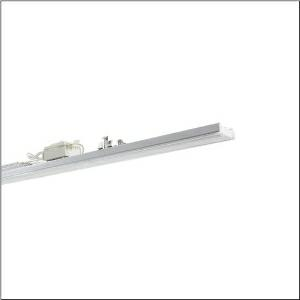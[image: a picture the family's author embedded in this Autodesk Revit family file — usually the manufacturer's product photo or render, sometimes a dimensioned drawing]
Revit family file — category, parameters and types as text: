
# Revit family: licross_11_recessed_ho_51tl1wmn4exm
name_source: partatom
category: Lighting Fixtures
units: mm (PartAtom-declared; Revit-internal decimal feet)

## family parameters
Cut with Voids When Loaded = No
Host = Face
Light Source = No
Part Type = Normal
Room Calculation Point = No
Round Connector Dimension = Use Diameter
Shared = No

## types (1)
- --- (1 x LED, 14240 lm, 74.5 W, 4000K)
    Apparent Load = 75 VA
    CIE Flux Codes = 73 94 99 100 100
    Color Rendering = 80
    Color Temperature = 4000K
    Default Elevation = 1800 mm
    Description = Licross 11 Recessed HO, luminaire insert, of sheet steel, coil coated, white, length: 1.500mm, width: 66mm, height: 67mm, LED rated luminous flux: 14.240lm, light colour: 840, SDCM (Standard Deviation of Colour Matching)MacAdam ≤ 2 SDCM (initial), control gear: ON/OFF Multilumen, with plug, 3-pole, with phase selection, mains connection: 220..240V, AC, 50/60Hz, rated input power: 75W, internal wiring halogen-free, primary optical cover: cover, of PMMA, light emission: direct distribution, primary light characteristic: symmetric, protection rating (complete): IP40, insulation class (complete): insulation class I (protective earthing), certification: CE, ENEC, VDE, UKCA, protection symbol: D if used in an environment without relevant dust loads with corresponding accessories, impact resistance: IK06, permissible ambient temperature for indoor applications: -35..+35°C, corresponds to IFS (International Featured Standards) requirements for safety and quality in the food industry, reducing of maximum allowable ambient temperature of 5°C with ceiling mounting, The light source and the operating device comply with the requirements of the Ecodesign Regulation (EU) 2019/2020 and are replaceable in accordance with this regulation, packaging unit: 1 piece
    Height = 58 mm
    Lamp = 1 x LED
    Lamp Light Flux = 14240 lm
    Lamp Power = 74.5 W
    Lamp count = 1
    Length = 1500 mm
    Luminous efficacy = 191 lm/W
    Manufacturer = Siteco
    ModVariant = No
    Model = 51TL1WMN4EXM
    Mounting Place = Ceiling
    Mounting Type = Pendant
    Number of Poles = 1
    OnlyDefault = Yes
    Power Factor = 1
    Product Name = Licross 11 Recessed HO
    Product group = luminaire insert | ceiling pendant
    ProductGroupID = 901
    Protection Class = Protection class I
    Protection Degree = IP 40
    RLX_Detail_Level = 1
    RLX_Emergency_Light_Flux = 0 lm
    RLX_Emergency_Type = 0
    RLX_Emergency_Type_DB = No
    RlxData = <blob elided: 22473 chars, md5=a01c1ca5>
    Socket = socket
    Standby Power = 0 W
    System Light Flux = 14240 lm
    System Power = 75 W
    Type Comments = factory setting: luminous flux: 100 % | (A | C | E) | 174 mA
    Type Image = l_1296930.jpg
    URL = http://relux.com
    VarID = @adj_065671
    Voltage = 0 V
    Weight = 0.00 kg
    Width = 66 mm

## geometry (parser evidence)
native form markers: Blend x4, Sweep x11
no freeform markers — native parametric forms only
